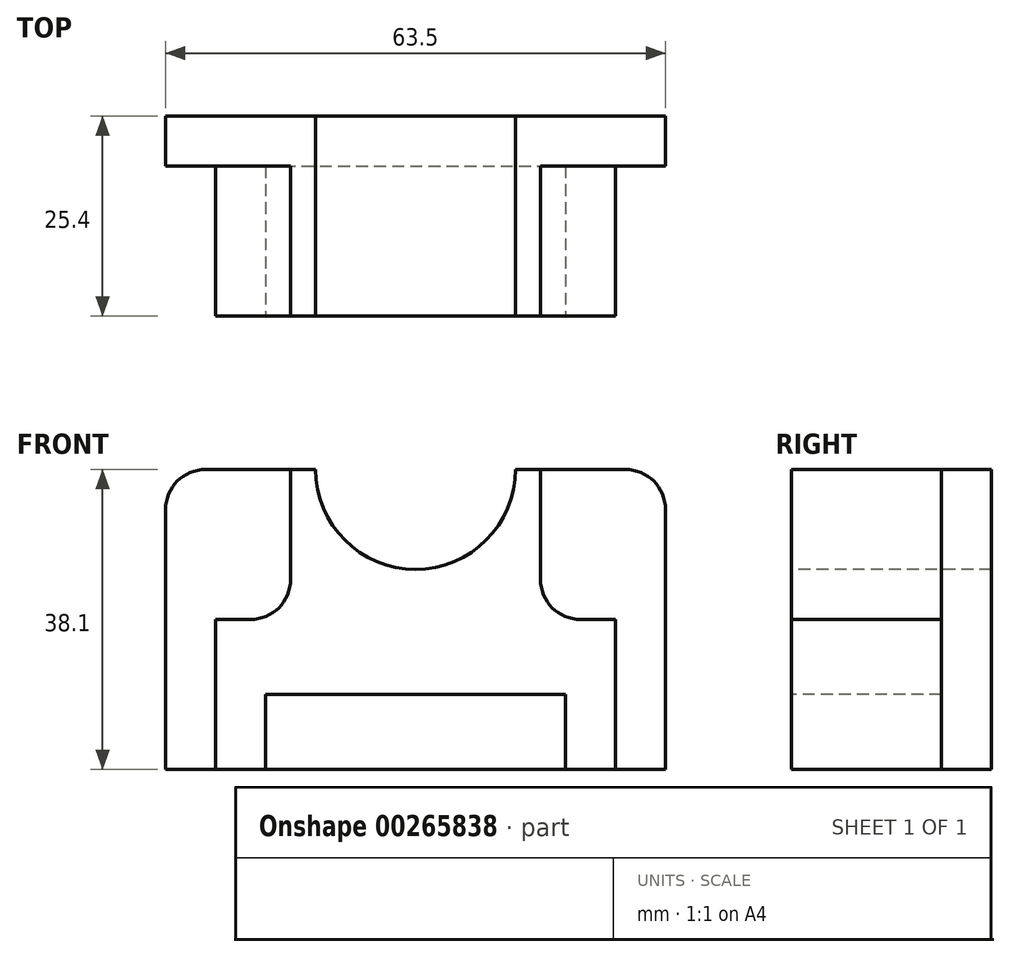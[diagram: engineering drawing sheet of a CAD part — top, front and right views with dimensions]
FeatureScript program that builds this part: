
annotation { "Feature Type Name" : "Feature", "Feature Type Description" : "" }
export const myFeature = defineFeature(function(context is Context, id is Id, definition is map)
    precondition{}
    {
        {
            var Q0;
            Q0=qCreatedBy(makeId("Front.planeOp"),FACE);
            var sketch = newSketch(context, id + "F0", { "sketchPlane" : qUnion([Q0])});
            skLineSegment(sketch, "E0.bottom", {"start": v(-24.7, 15.71) * mm, "end": v(38.8, 15.71) * mm});
            skLineSegment(sketch, "E0.top", {"start": v(-24.7, -22.39) * mm, "end": v(38.8, -22.39) * mm});
            skLineSegment(sketch, "E0.left", {"start": v(-24.7, 15.71) * mm, "end": v(-24.7, -22.39) * mm});
            skLineSegment(sketch, "E0.right", {"start": v(38.8, 15.71) * mm, "end": v(38.8, -22.39) * mm});
            skSolve(sketch);
        }
        {
            var Q0;
            Q0 = qSketchRegion(id + "F0", true);
            extrude(context, id + "F1", {"entities" : qUnion([Q0]), "depth" : 25.4 * mm});
        }
        {
            var Q0;
            Q0=makeQuery(id+"F1.opExtrude","CAP_FACE",FACE,{"disambiguationData":[OSD([sQuery(id+"F0.wireOp",EDGE,"E0.bottom"),sQuery(id+"F0.wireOp",EDGE,"E0.top"),sQuery(id+"F0.wireOp",EDGE,"E0.left"),sQuery(id+"F0.wireOp",EDGE,"E0.right")])],"isStart":false});
            var sketch = newSketch(context, id + "F2", { "sketchPlane" : qUnion([Q0])});
            skCircle(sketch, "E1", {"center": v(7.06, 15.71) * mm, "radius": 12.7 * mm});
            skSolve(sketch);
        }
        {
            var Q0;
            Q0 = qSketchRegion(id + "F2", true);
            extrude(context, id + "F3", {"entities" : qUnion([Q0]), "operationType" : NewBodyOperationType.REMOVE, "oppositeDirection" : true, "depth" : 25.4 * mm});
        }
        {
            var Q0;
            Q0=makeQuery(id+"F1.opExtrude","CAP_FACE",FACE,{"disambiguationData":[OSD([sQuery(id+"F0.wireOp",EDGE,"E0.bottom"),sQuery(id+"F0.wireOp",EDGE,"E0.top"),sQuery(id+"F0.wireOp",EDGE,"E0.left"),sQuery(id+"F0.wireOp",EDGE,"E0.right")])],"isStart":false});
            var sketch = newSketch(context, id + "F4", { "sketchPlane" : qUnion([Q0])});
            skLineSegment(sketch, "E2.bottom", {"start": v(-18.34, 15.71) * mm, "end": v(-24.7, 15.71) * mm});
            skLineSegment(sketch, "E2.top", {"start": v(-18.34, -22.39) * mm, "end": v(-24.7, -22.39) * mm});
            skLineSegment(sketch, "E2.left", {"start": v(-18.34, 15.71) * mm, "end": v(-18.34, -22.39) * mm});
            skLineSegment(sketch, "E2.right", {"start": v(-24.7, 15.71) * mm, "end": v(-24.7, -22.39) * mm});
            skLineSegment(sketch, "E3.bottom", {"start": v(32.46, 15.71) * mm, "end": v(38.8, 15.71) * mm});
            skLineSegment(sketch, "E3.top", {"start": v(32.46, -22.39) * mm, "end": v(38.8, -22.39) * mm});
            skLineSegment(sketch, "E3.left", {"start": v(32.46, 15.71) * mm, "end": v(32.46, -22.39) * mm});
            skLineSegment(sketch, "E3.right", {"start": v(38.8, 15.71) * mm, "end": v(38.8, -22.39) * mm});
            skLineSegment(sketch, "E4.bottom", {"start": v(-12, -12.86) * mm, "end": v(26.1, -12.86) * mm});
            skLineSegment(sketch, "E4.top", {"start": v(-12, -22.39) * mm, "end": v(26.1, -22.39) * mm});
            skLineSegment(sketch, "E4.left", {"start": v(-12, -12.86) * mm, "end": v(-12, -22.39) * mm});
            skLineSegment(sketch, "E4.right", {"start": v(26.1, -12.86) * mm, "end": v(26.1, -22.39) * mm});
            skLineSegment(sketch, "E5.bottom", {"start": v(22.93, 15.71) * mm, "end": v(32.46, 15.71) * mm});
            skLineSegment(sketch, "E5.top", {"start": v(22.93, -3.34) * mm, "end": v(32.46, -3.34) * mm});
            skLineSegment(sketch, "E5.left", {"start": v(22.93, 15.71) * mm, "end": v(22.93, -3.34) * mm});
            skLineSegment(sketch, "E5.right", {"start": v(32.46, 15.71) * mm, "end": v(32.46, -3.34) * mm});
            skLineSegment(sketch, "E6.bottom", {"start": v(-8.82, 15.71) * mm, "end": v(-18.34, 15.71) * mm});
            skLineSegment(sketch, "E6.top", {"start": v(-8.82, -3.34) * mm, "end": v(-18.34, -3.34) * mm});
            skLineSegment(sketch, "E6.left", {"start": v(-8.82, 15.71) * mm, "end": v(-8.82, -3.34) * mm});
            skLineSegment(sketch, "E6.right", {"start": v(-18.34, 15.71) * mm, "end": v(-18.34, -3.34) * mm});
            skSolve(sketch);
        }
        {
            var Q0;
            Q0=makeQuery(id+"F4.imprint","IMPRINT",FACE,{"disambiguationData":[TD([[makeQuery(id+"F4.imprint","IMPRINT",EDGE,{"derivedFrom":sQuery(id+"F4.wireOp",EDGE,"E3.bottom")}),-1.0]])]});
            extrude(context, id + "F5", {"entities" : qUnion([Q0]), "operationType" : NewBodyOperationType.REMOVE, "oppositeDirection" : true, "depth" : 19.05 * mm});
        }
        {
            var Q0;
            Q0=makeQuery(id+"F4.imprint","IMPRINT",FACE,{"disambiguationData":[TD([[makeQuery(id+"F4.imprint","IMPRINT",EDGE,{"derivedFrom":sQuery(id+"F4.wireOp",EDGE,"E2.bottom")}),-1.0]])]});
            extrude(context, id + "F6", {"entities" : qUnion([Q0]), "operationType" : NewBodyOperationType.REMOVE, "oppositeDirection" : true, "depth" : 19.05 * mm});
        }
        {
            var Q0;
            Q0=makeQuery(id+"F4.imprint","IMPRINT",FACE,{"disambiguationData":[TD([[makeQuery(id+"F4.imprint","IMPRINT",EDGE,{"derivedFrom":sQuery(id+"F4.wireOp",EDGE,"E4.bottom")}),-1.0]])]});
            extrude(context, id + "F7", {"entities" : qUnion([Q0]), "operationType" : NewBodyOperationType.REMOVE, "oppositeDirection" : true, "depth" : 19.05 * mm});
        }
        {
            var Q0;
            Q0=makeQuery(id+"F4.imprint","IMPRINT",FACE,{"disambiguationData":[TD([[makeQuery(id+"F4.imprint","IMPRINT",EDGE,{"derivedFrom":sQuery(id+"F4.wireOp",EDGE,"E6.bottom")}),-1.0]])]});
            extrude(context, id + "F8", {"entities" : qUnion([Q0]), "operationType" : NewBodyOperationType.REMOVE, "oppositeDirection" : true, "depth" : 19.05 * mm});
        }
        {
            var Q0;
            Q0=makeQuery(id+"F4.imprint","IMPRINT",FACE,{"disambiguationData":[TD([[makeQuery(id+"F4.imprint","IMPRINT",EDGE,{"derivedFrom":sQuery(id+"F4.wireOp",EDGE,"E5.bottom")}),-1.0]])]});
            extrude(context, id + "F9", {"entities" : qUnion([Q0]), "operationType" : NewBodyOperationType.REMOVE, "oppositeDirection" : true, "depth" : 19.05 * mm});
        }
        {
            var Q0;
            Q0=makeQuery(id+"F1.opExtrude","SWEPT_EDGE",EDGE,{"disambiguationData":[OSD([sQuery(id+"F0.wireOp",EDGE,"E0.bottom"),sQuery(id+"F0.wireOp",EDGE,"E0.left")])]});
            var Q1;
            Q1=makeQuery(id+"F1.opExtrude","SWEPT_EDGE",EDGE,{"disambiguationData":[OSD([sQuery(id+"F0.wireOp",EDGE,"E0.bottom"),sQuery(id+"F0.wireOp",EDGE,"E0.right")])]});
            var Q2;
            Q2=makeQuery(id+"F9.boolean.opBoolean","COPY",EDGE,{"derivedFrom":makeQuery(id+"F9.opExtrude","SWEPT_EDGE",EDGE,{"disambiguationData":[OSD([sQuery(id+"F4.wireOp",EDGE,"E5.top"),sQuery(id+"F4.wireOp",EDGE,"E5.left")])]})});
            var Q3;
            Q3=makeQuery(id+"F8.boolean.opBoolean","COPY",EDGE,{"derivedFrom":makeQuery(id+"F8.opExtrude","SWEPT_EDGE",EDGE,{"disambiguationData":[OSD([sQuery(id+"F4.wireOp",EDGE,"E6.top"),sQuery(id+"F4.wireOp",EDGE,"E6.left")])]})});
            fillet(context, id + "F10", {"entities" : qUnion([Q0, Q1, Q2, Q3]), "radius" : 5.08 * mm, "tangentPropagation" : true, "allowEdgeOverflow" : false});
        }
    });
